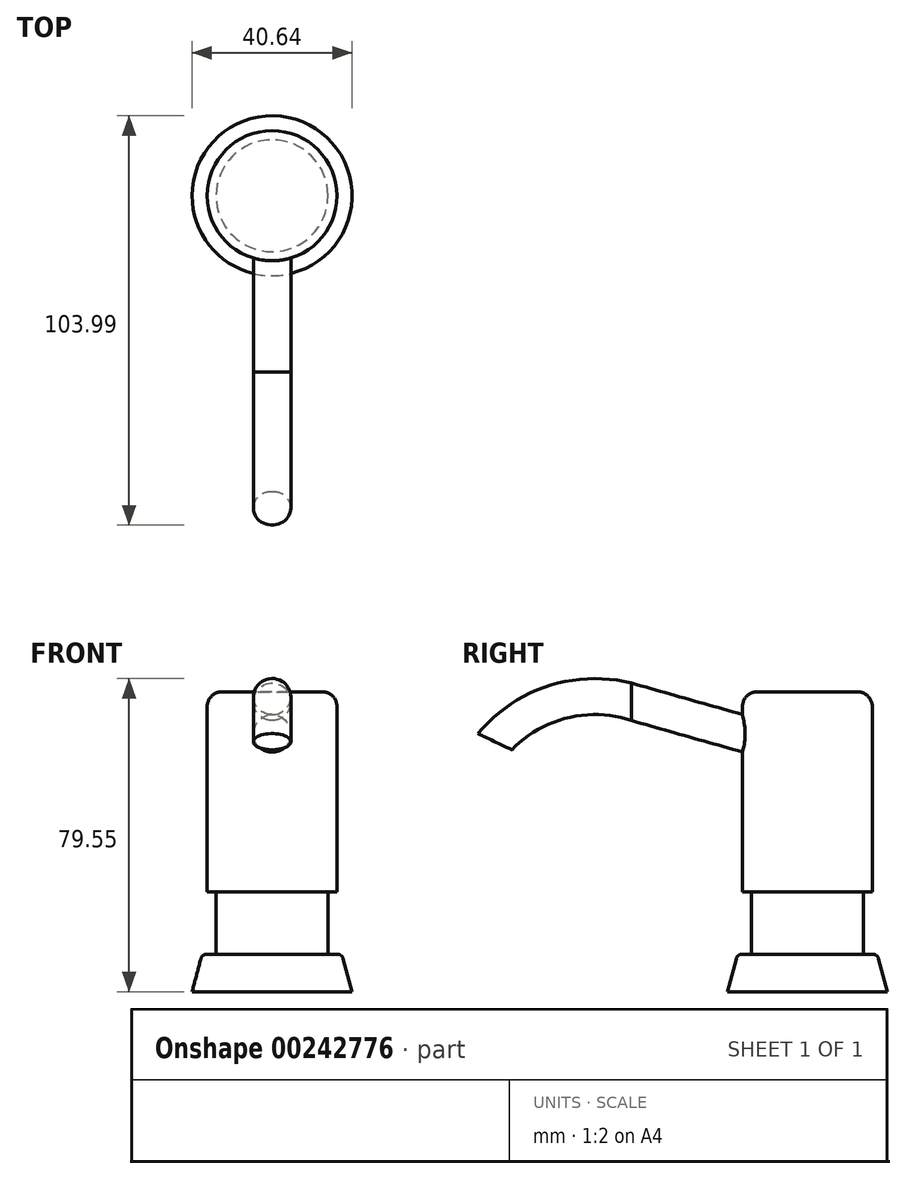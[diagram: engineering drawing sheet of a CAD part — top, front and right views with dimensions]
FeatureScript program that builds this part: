
annotation { "Feature Type Name" : "Feature", "Feature Type Description" : "" }
export const myFeature = defineFeature(function(context is Context, id is Id, definition is map)
    precondition{}
    {
        {
            var Q0;
            Q0=qCreatedBy(makeId("Front.planeOp"),FACE);
            var sketch = newSketch(context, id + "F0", { "sketchPlane" : qUnion([Q0])});
            skLineSegment(sketch, "E0", {"start": v(0, 0) * mm, "end": v(0, 76.2) * mm});
            skLineSegment(sketch, "E1", {"start": v(0, 76.2) * mm, "end": v(16.51, 76.2) * mm});
            skLineSegment(sketch, "E2", {"start": v(16.51, 76.2) * mm, "end": v(16.51, 25.4) * mm});
            skLineSegment(sketch, "E3", {"start": v(16.51, 25.4) * mm, "end": v(14.22, 25.4) * mm});
            skLineSegment(sketch, "E4", {"start": v(14.22, 25.4) * mm, "end": v(14.22, 9.52) * mm});
            skLineSegment(sketch, "E5", {"start": v(14.22, 9.52) * mm, "end": v(17.78, 9.52) * mm});
            skLineSegment(sketch, "E6", {"start": v(17.78, 9.52) * mm, "end": v(20.32, 0) * mm});
            skLineSegment(sketch, "E7", {"start": v(20.32, 0) * mm, "end": v(0, 0) * mm});
            skSolve(sketch);
        }
        {
            var Q0;
            Q0=makeQuery(id+"F0.imprint","IMPRINT",FACE,{"disambiguationData":[TD([[makeQuery(id+"F0.imprint","IMPRINT",EDGE,{"derivedFrom":sQuery(id+"F0.wireOp",EDGE,"E0")}),-1.0]])]});
            var Q1;
            Q1 = qConstructionFilter(qBodyType(qCreatedBy(id + "F0" ,EDGE), BodyType.WIRE), ConstructionObject.NO);
            var Q2;
            Q2=sQuery(id+"F0.wireOp",EDGE,"E0");
            revolve(context, id + "F1", {"entities" : qUnion([Q0]), "surfaceEntities" : qUnion([Q1]), "axis" : qUnion([Q2]), "revolveType" : RevolveType.FULL});
        }
        {
            var Q0;
            Q0=makeQuery(id+"F1.opRevolve","SWEPT_EDGE",EDGE,{"disambiguationData":[OSD([sQuery(id+"F0.wireOp",EDGE,"E1"),sQuery(id+"F0.wireOp",EDGE,"E2")])]});
            fillet(context, id + "F2", {"entities" : qUnion([Q0]), "radius" : 3.8 * mm, "tangentPropagation" : true, "allowEdgeOverflow" : false});
        }
        {
            var Q0;
            Q0=makeQuery(id+"F1.opRevolve","SWEPT_EDGE",EDGE,{"disambiguationData":[OSD([sQuery(id+"F0.wireOp",EDGE,"E5"),sQuery(id+"F0.wireOp",EDGE,"E6")])]});
            fillet(context, id + "F3", {"entities" : qUnion([Q0]), "radius" : 1.52 * mm, "tangentPropagation" : true, "allowEdgeOverflow" : false});
        }
        {
            var Q0;
            Q0=qCreatedBy(makeId("Right.planeOp"),FACE);
            var sketch = newSketch(context, id + "F4", { "sketchPlane" : qUnion([Q0])});
            skLineSegment(sketch, "E8", {"start": v(0, 60.96) * mm, "end": v(-44.74, 73.66) * mm});
            skArc(sketch, "E9", {"start": v(-44.74, 73.66) * mm, "mid": v(-63.52, 73.58) * mm, "end": v(-79.38, 63.5) * mm});
            skSolve(sketch);
        }
        {
            var Q0;
            Q0=qCreatedBy(makeId("Front.planeOp"),FACE);
            var sketch = newSketch(context, id + "F5", { "sketchPlane" : qUnion([Q0])});
            skCircle(sketch, "E10", {"center": v(0, 60.96) * mm, "radius": 4.76 * mm});
            skSolve(sketch);
        }
        {
            var Q0;
            Q0 = qSketchRegion(id + "F5", true);
            var Q1;
            Q1 = qConstructionFilter(qBodyType(qCreatedBy(id + "F4" ,EDGE), BodyType.WIRE), ConstructionObject.NO);
            sweep(context, id + "F6", {"operationType" : NewBodyOperationType.ADD, "profiles" : qUnion([Q0]), "path" : qUnion([Q1])});
        }
    });
